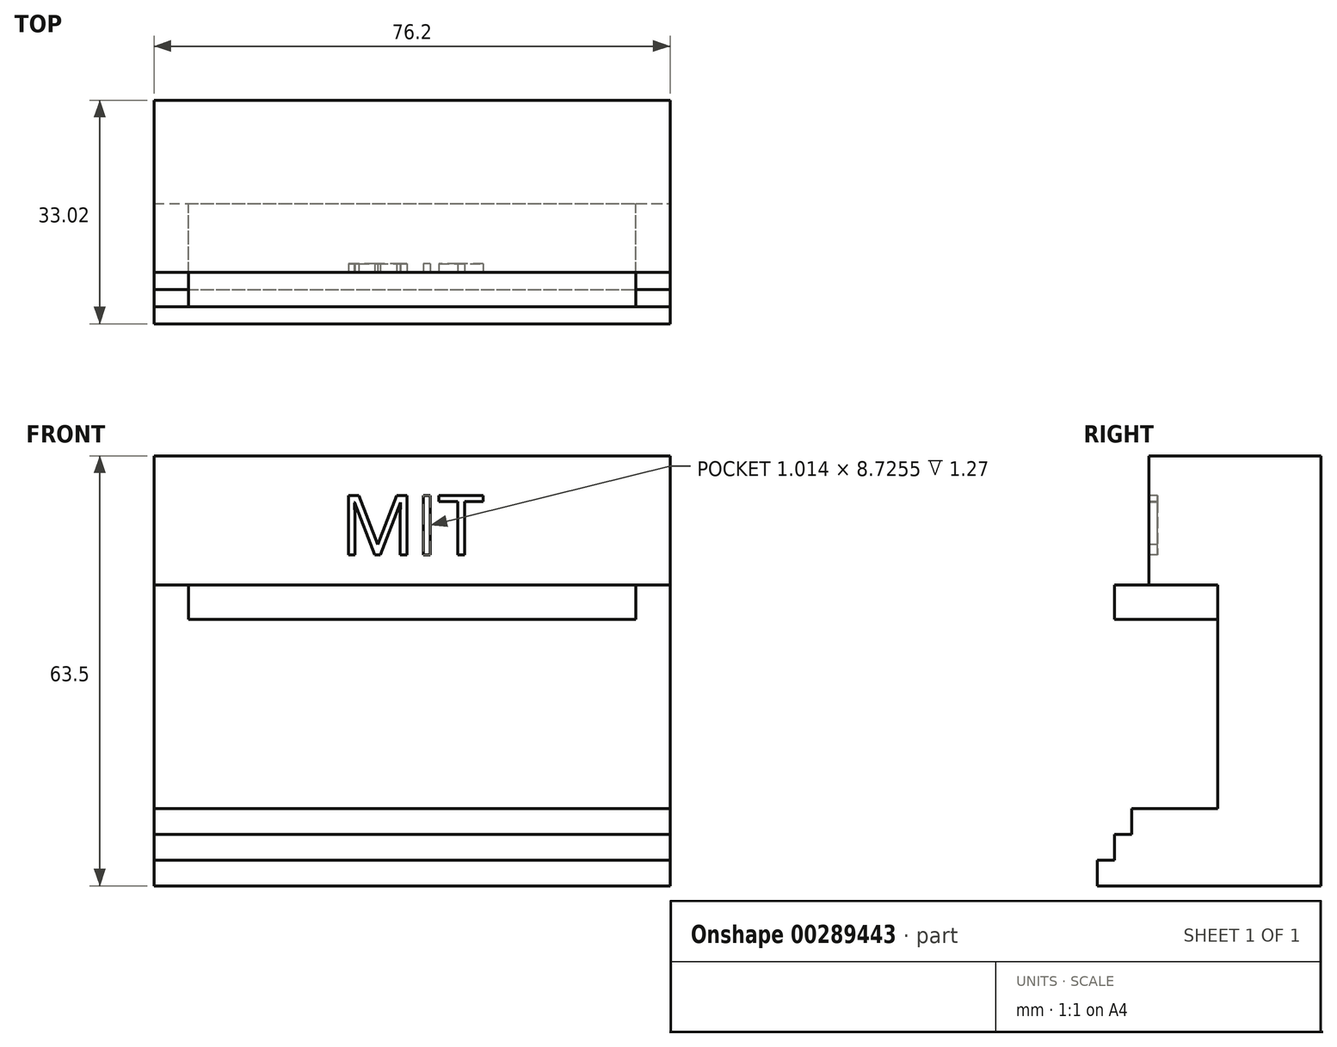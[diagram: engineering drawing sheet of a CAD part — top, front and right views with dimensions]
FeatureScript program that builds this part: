
annotation { "Feature Type Name" : "Feature", "Feature Type Description" : "" }
export const myFeature = defineFeature(function(context is Context, id is Id, definition is map)
    precondition{}
    {
        {
            var Q0;
            Q0=qCreatedBy(makeId("Top.planeOp"),FACE);
            var sketch = newSketch(context, id + "F0", { "sketchPlane" : qUnion([Q0])});
            skLineSegment(sketch, "E0.bottom", {"start": v(-38.1, 12.7) * mm, "end": v(38.1, 12.7) * mm});
            skLineSegment(sketch, "E0.top", {"start": v(-38.1, -12.7) * mm, "end": v(38.1, -12.7) * mm});
            skLineSegment(sketch, "E0.left", {"start": v(-38.1, 12.7) * mm, "end": v(-38.1, -12.7) * mm});
            skLineSegment(sketch, "E0.right", {"start": v(38.1, 12.7) * mm, "end": v(38.1, -12.7) * mm});
            skSolve(sketch);
        }
        {
            var Q0;
            Q0=makeQuery(id+"F0.imprint","IMPRINT",FACE,{"disambiguationData":[TD([[makeQuery(id+"F0.imprint","IMPRINT",EDGE,{"derivedFrom":sQuery(id+"F0.wireOp",EDGE,"E0.bottom")}),-1.0]])]});
            extrude(context, id + "F1", {"entities" : qUnion([Q0]), "depth" : 63.5 * mm});
        }
        {
            var Q0;
            Q0=makeQuery(id+"F1.opExtrude","SWEPT_FACE",FACE,{"disambiguationData":[OSD([sQuery(id+"F0.wireOp",EDGE,"E0.top")])]});
            var sketch = newSketch(context, id + "F2", { "sketchPlane" : qUnion([Q0])});
            skLineSegment(sketch, "E1.bottom", {"start": v(-38.1, 44.45) * mm, "end": v(38.1, 44.45) * mm});
            skLineSegment(sketch, "E1.top", {"start": v(-38.1, 11.43) * mm, "end": v(38.1, 11.43) * mm});
            skLineSegment(sketch, "E1.left", {"start": v(-38.1, 44.45) * mm, "end": v(-38.1, 11.43) * mm});
            skLineSegment(sketch, "E1.right", {"start": v(38.1, 44.45) * mm, "end": v(38.1, 11.43) * mm});
            skSolve(sketch);
        }
        {
            var Q0;
            Q0=makeQuery(id+"F2.imprint","IMPRINT",FACE,{"disambiguationData":[TD([[makeQuery(id+"F2.imprint","IMPRINT",EDGE,{"derivedFrom":sQuery(id+"F2.wireOp",EDGE,"E1.bottom")}),-1.0]])]});
            extrude(context, id + "F3", {"entities" : qUnion([Q0]), "operationType" : NewBodyOperationType.REMOVE, "oppositeDirection" : true, "depth" : 10.16 * mm});
        }
        {
            var Q0;
            {var subQ2=sQuery(id+"F0.wireOp",EDGE,"E0.top");Q0=makeQuery(id+"F3.boolean.opBoolean","SPLIT",FACE,{"disambiguationData":[TD([makeQuery(id+"F3.opExtrude","SWEPT_FACE",FACE,{"disambiguationData":[OSD([sQuery(id+"F2.wireOp",EDGE,"E1.top")])]})])],"derivedFrom":makeQuery(id+"F1.opExtrude","SWEPT_FACE",FACE,{"disambiguationData":[OSD([subQ2])]})});}
            var sketch = newSketch(context, id + "F4", { "sketchPlane" : qUnion([Q0])});
            skLineSegment(sketch, "E2.bottom", {"start": v(-38.1, 11.43) * mm, "end": v(38.1, 11.43) * mm});
            skLineSegment(sketch, "E2.top", {"start": v(-38.1, 7.62) * mm, "end": v(38.1, 7.62) * mm});
            skLineSegment(sketch, "E2.left", {"start": v(-38.1, 11.43) * mm, "end": v(-38.1, 7.62) * mm});
            skLineSegment(sketch, "E2.right", {"start": v(38.1, 11.43) * mm, "end": v(38.1, 7.62) * mm});
            skSolve(sketch);
        }
        {
            var Q0;
            Q0=makeQuery(id+"F4.imprint","IMPRINT",FACE,{"disambiguationData":[TD([[makeQuery(id+"F4.imprint","IMPRINT",EDGE,{"derivedFrom":sQuery(id+"F4.wireOp",EDGE,"E2.bottom")}),-1.0]])]});
            extrude(context, id + "F5", {"entities" : qUnion([Q0]), "operationType" : NewBodyOperationType.ADD, "depth" : 2.54 * mm});
        }
        {
            var Q0;
            {var subQ2=sQuery(id+"F0.wireOp",EDGE,"E0.top");Q0=makeQuery(id+"F3.boolean.opBoolean","SPLIT",FACE,{"disambiguationData":[TD([makeQuery(id+"F3.opExtrude","SWEPT_FACE",FACE,{"disambiguationData":[OSD([sQuery(id+"F2.wireOp",EDGE,"E1.top")])]})])],"derivedFrom":makeQuery(id+"F1.opExtrude","SWEPT_FACE",FACE,{"disambiguationData":[OSD([subQ2])]})});}
            var sketch = newSketch(context, id + "F6", { "sketchPlane" : qUnion([Q0])});
            skLineSegment(sketch, "E3.bottom", {"start": v(-38.1, 7.62) * mm, "end": v(38.1, 7.62) * mm});
            skLineSegment(sketch, "E3.top", {"start": v(-38.1, 3.81) * mm, "end": v(38.1, 3.81) * mm});
            skLineSegment(sketch, "E3.left", {"start": v(-38.1, 7.62) * mm, "end": v(-38.1, 3.81) * mm});
            skLineSegment(sketch, "E3.right", {"start": v(38.1, 7.62) * mm, "end": v(38.1, 3.81) * mm});
            skSolve(sketch);
        }
        {
            var Q0;
            Q0=makeQuery(id+"F6.imprint","IMPRINT",FACE,{"disambiguationData":[TD([[makeQuery(id+"F6.imprint","IMPRINT",EDGE,{"derivedFrom":sQuery(id+"F6.wireOp",EDGE,"E3.bottom")}),-1.0]])]});
            extrude(context, id + "F7", {"entities" : qUnion([Q0]), "operationType" : NewBodyOperationType.ADD, "depth" : 5.08 * mm});
        }
        {
            var Q0;
            {var subQ2=sQuery(id+"F0.wireOp",EDGE,"E0.top");Q0=makeQuery(id+"F3.boolean.opBoolean","SPLIT",FACE,{"disambiguationData":[TD([makeQuery(id+"F3.opExtrude","SWEPT_FACE",FACE,{"disambiguationData":[OSD([sQuery(id+"F2.wireOp",EDGE,"E1.top")])]})])],"derivedFrom":makeQuery(id+"F1.opExtrude","SWEPT_FACE",FACE,{"disambiguationData":[OSD([subQ2])]})});}
            var sketch = newSketch(context, id + "F8", { "sketchPlane" : qUnion([Q0])});
            skLineSegment(sketch, "E4.bottom", {"start": v(-38.1, 3.81) * mm, "end": v(38.1, 3.81) * mm});
            skLineSegment(sketch, "E4.top", {"start": v(-38.1, 0) * mm, "end": v(38.1, 0) * mm});
            skLineSegment(sketch, "E4.left", {"start": v(-38.1, 3.81) * mm, "end": v(-38.1, 0) * mm});
            skLineSegment(sketch, "E4.right", {"start": v(38.1, 3.81) * mm, "end": v(38.1, 0) * mm});
            skSolve(sketch);
        }
        {
            var Q0;
            Q0=makeQuery(id+"F3.boolean.opBoolean","COPY",FACE,{"derivedFrom":makeQuery(id+"F3.opExtrude","CAP_FACE",FACE,{"disambiguationData":[OSD([sQuery(id+"F2.wireOp",EDGE,"E1.bottom"),sQuery(id+"F2.wireOp",EDGE,"E1.top"),sQuery(id+"F2.wireOp",EDGE,"E1.left"),sQuery(id+"F2.wireOp",EDGE,"E1.right")])],"isStart":false})});
            var sketch = newSketch(context, id + "F9", { "sketchPlane" : qUnion([Q0])});
            skLineSegment(sketch, "E5.bottom", {"start": v(-33.02, 44.45) * mm, "end": v(33.02, 44.45) * mm});
            skLineSegment(sketch, "E5.top", {"start": v(-33.02, 39.37) * mm, "end": v(33.02, 39.37) * mm});
            skLineSegment(sketch, "E5.left", {"start": v(-33.02, 44.45) * mm, "end": v(-33.02, 39.37) * mm});
            skLineSegment(sketch, "E5.right", {"start": v(33.02, 44.45) * mm, "end": v(33.02, 39.37) * mm});
            skSolve(sketch);
        }
        {
            var Q0;
            Q0=makeQuery(id+"F9.imprint","IMPRINT",FACE,{"disambiguationData":[TD([[makeQuery(id+"F9.imprint","IMPRINT",EDGE,{"derivedFrom":sQuery(id+"F9.wireOp",EDGE,"E5.bottom")}),-1.0]])]});
            extrude(context, id + "F10", {"entities" : qUnion([Q0]), "operationType" : NewBodyOperationType.ADD, "depth" : 15.24 * mm});
        }
        {
            var Q0;
            Q0 = qSketchRegion(id + "F8", true);
            extrude(context, id + "F11", {"entities" : qUnion([Q0]), "operationType" : NewBodyOperationType.ADD, "depth" : 7.62 * mm});
        }
        {
            var Q0;
            {var subQ2=sQuery(id+"F0.wireOp",EDGE,"E0.top");Q0=makeQuery(id+"F3.boolean.opBoolean","SPLIT",FACE,{"disambiguationData":[TD([makeQuery(id+"F3.opExtrude","SWEPT_FACE",FACE,{"disambiguationData":[OSD([sQuery(id+"F2.wireOp",EDGE,"E1.bottom")])]})])],"derivedFrom":makeQuery(id+"F1.opExtrude","SWEPT_FACE",FACE,{"disambiguationData":[OSD([subQ2])]})});}
            var sketch = newSketch(context, id + "F12", { "sketchPlane" : qUnion([Q0])});
            skText(sketch, "E6", { "text": "MIT", "fontName": "OpenSans-Regular.ttf"});
            const initialGuessF12  = {"E6": [-0.01057, 0.04889, 1, 0, 0.0088]};
            skSetInitialGuess(sketch, initialGuessF12);
            skSolve(sketch);
        }
        {
            var Q0;
            Q0 = qSketchRegion(id + "F12", true);
            extrude(context, id + "F13", {"entities" : qUnion([Q0]), "operationType" : NewBodyOperationType.REMOVE, "oppositeDirection" : true, "depth" : 1.27 * mm});
        }
    });
